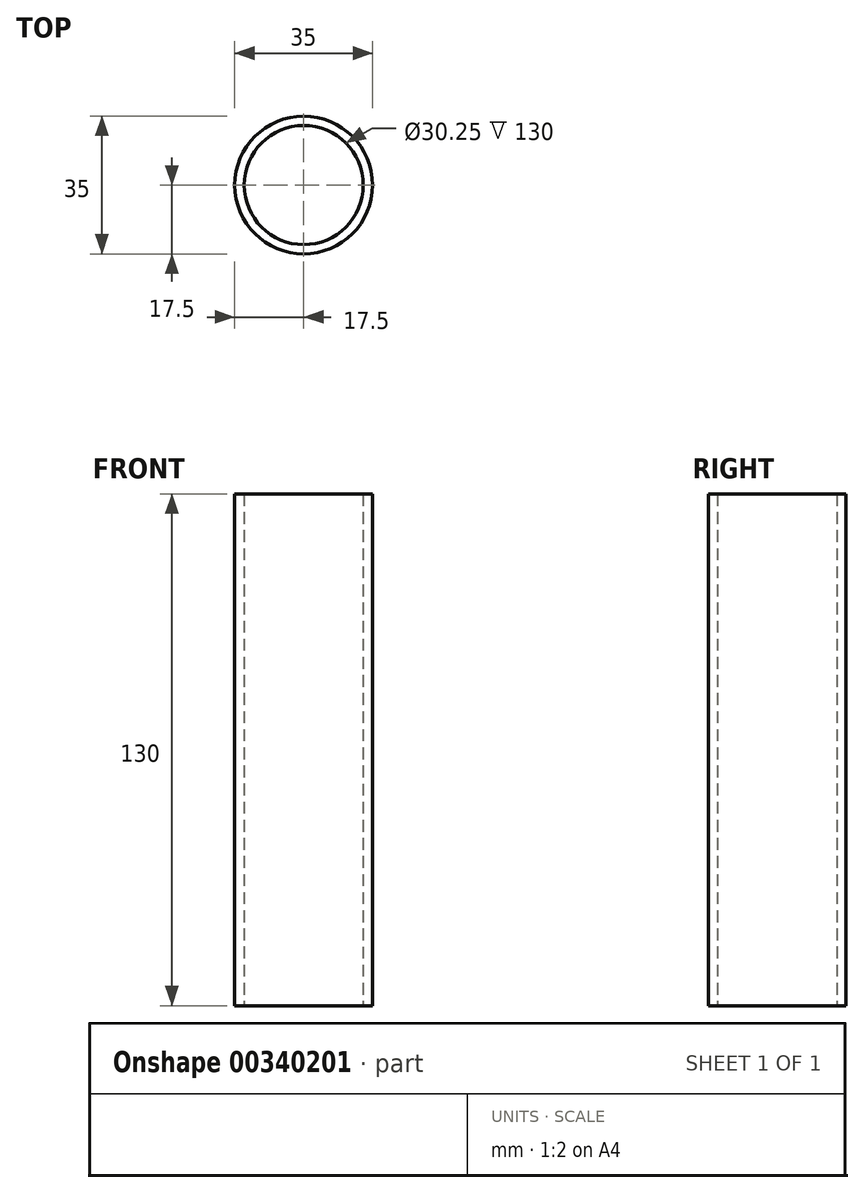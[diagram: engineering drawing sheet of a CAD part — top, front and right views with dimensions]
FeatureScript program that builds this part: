
annotation { "Feature Type Name" : "Feature", "Feature Type Description" : "" }
export const myFeature = defineFeature(function(context is Context, id is Id, definition is map)
    precondition{}
    {
        {
            var Q0;
            Q0=qCreatedBy(makeId("Top.planeOp"),FACE);
            var sketch = newSketch(context, id + "F0", { "sketchPlane" : qUnion([Q0])});
            skCircle(sketch, "E0", {"center": v(0, 0) * mm, "radius": 17.5 * mm});
            skSolve(sketch);
        }
        {
            var Q0;
            Q0=makeQuery(id+"F0.imprint","IMPRINT",FACE,{"disambiguationData":[TD([[makeQuery(id+"F0.imprint","IMPRINT",EDGE,{"derivedFrom":sQuery(id+"F0.wireOp",EDGE,"E0")}),1.0]])]});
            extrude(context, id + "F1", {"entities" : qUnion([Q0]), "depth" : 130 * mm});
        }
        {
            var Q0;
            Q0=qCreatedBy(makeId("Top.planeOp"),FACE);
            var sketch = newSketch(context, id + "F2", { "sketchPlane" : qUnion([Q0])});
            skCircle(sketch, "E1", {"center": v(0, 0) * mm, "radius": 15.12 * mm});
            skSolve(sketch);
        }
        {
            var Q0;
            Q0=makeQuery(id+"F2.imprint","IMPRINT",FACE,{"disambiguationData":[TD([[makeQuery(id+"F2.imprint","IMPRINT",EDGE,{"derivedFrom":sQuery(id+"F2.wireOp",EDGE,"E1")}),1.0]])]});
            extrude(context, id + "F3", {"entities" : qUnion([Q0]), "operationType" : NewBodyOperationType.REMOVE, "endBound" : BoundingType.THROUGH_ALL, "depth" : 25 * mm});
        }
    });
